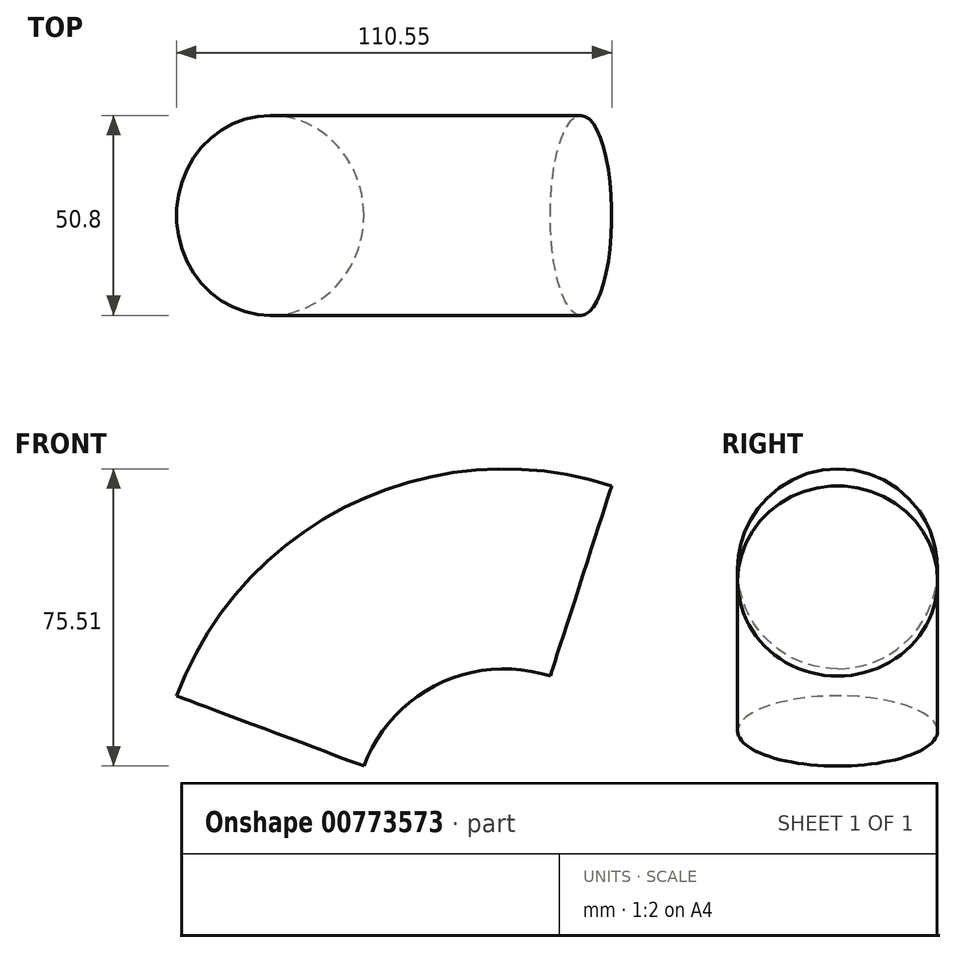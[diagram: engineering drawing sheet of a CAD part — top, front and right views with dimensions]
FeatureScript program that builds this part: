
annotation { "Feature Type Name" : "Feature", "Feature Type Description" : "" }
export const myFeature = defineFeature(function(context is Context, id is Id, definition is map)
    precondition{}
    {
        {
            var Q0;
            Q0=qCreatedBy(makeId("Front.planeOp"),FACE);
            var sketch = newSketch(context, id + "F0", { "sketchPlane" : qUnion([Q0])});
            skArc(sketch, "E0", {"start": v(-59.45, 22.32) * mm, "mid": v(-27.6, 57.19) * mm, "end": v(19.51, 60.43) * mm});
            skSolve(sketch);
        }
        {
            var Q0;
            Q0=qCreatedBy(makeId("Right.planeOp"),FACE);
            var sketch = newSketch(context, id + "F1", { "sketchPlane" : qUnion([Q0])});
            skCircle(sketch, "E1", {"center": v(0, 63.5) * mm, "radius": 25.4 * mm});
            skSolve(sketch);
        }
        {
            var Q0;
            Q0=makeQuery(id+"F1.imprint","IMPRINT",FACE,{"disambiguationData":[TD([[makeQuery(id+"F1.imprint","IMPRINT",EDGE,{"derivedFrom":sQuery(id+"F1.wireOp",EDGE,"E1")}),1.0]])]});
            var Q1;
            Q1=sQuery(id+"F0.wireOp",EDGE,"E0");
            sweep(context, id + "F2", {"profiles" : qUnion([Q0]), "path" : qUnion([Q1])});
        }
    });
